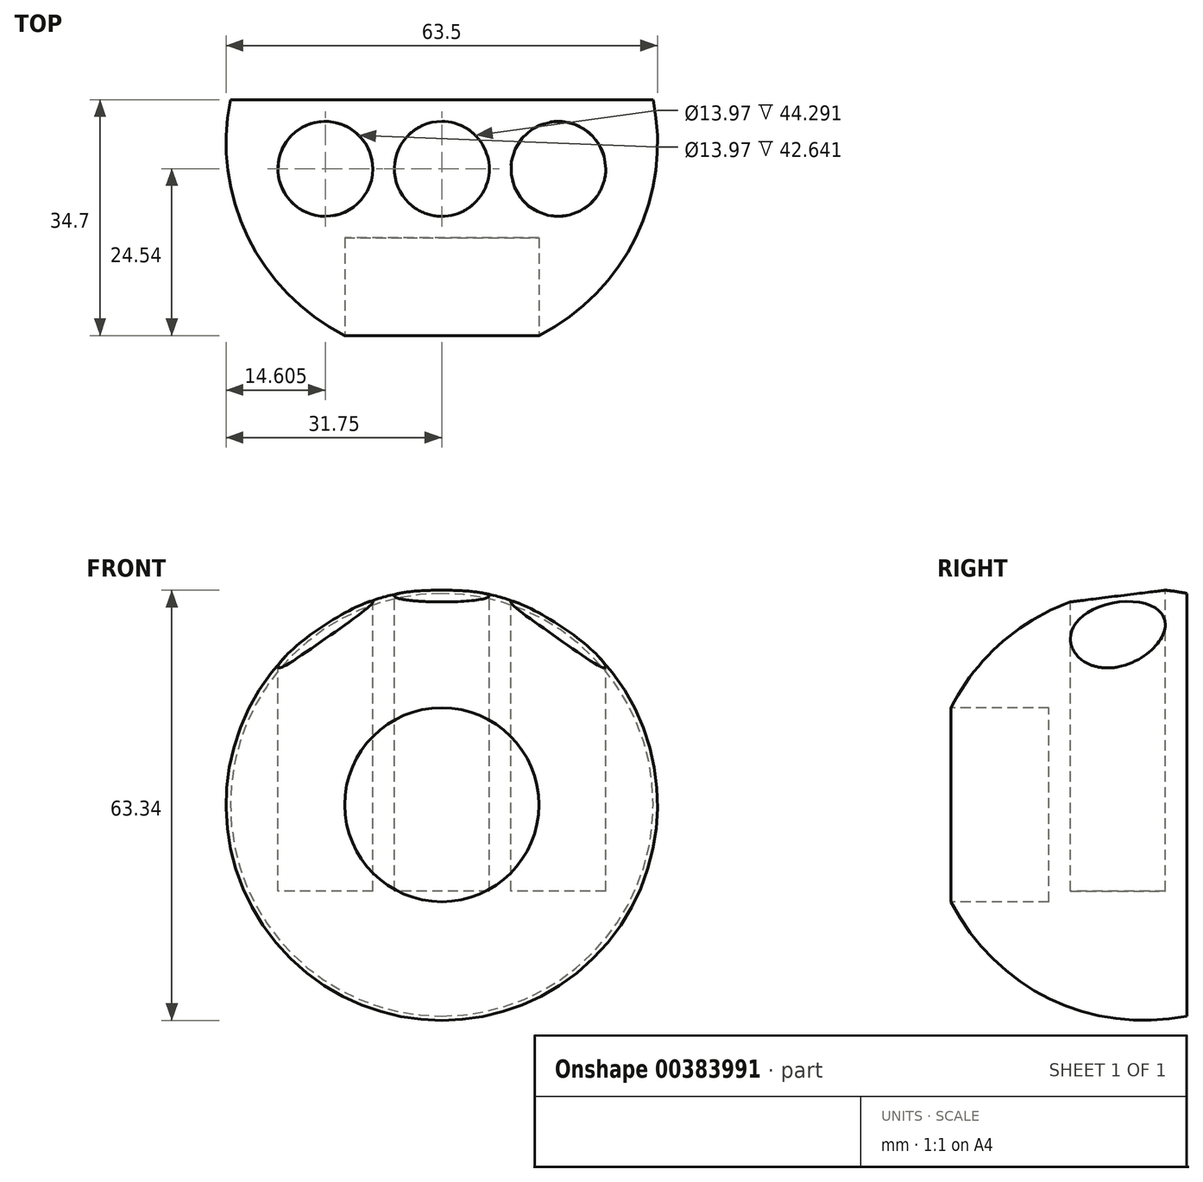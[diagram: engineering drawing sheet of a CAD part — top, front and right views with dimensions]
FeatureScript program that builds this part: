
annotation { "Feature Type Name" : "Feature", "Feature Type Description" : "" }
export const myFeature = defineFeature(function(context is Context, id is Id, definition is map)
    precondition{}
    {
        {
            var Q0;
            Q0=qCreatedBy(makeId("Top.planeOp"),FACE);
            var sketch = newSketch(context, id + "F0", { "sketchPlane" : qUnion([Q0])});
            skCircle(sketch, "E0", {"center": v(0, 0) * mm, "radius": 31.75 * mm});
            skLineSegment(sketch, "E1", {"start": v(0, 31.75) * mm, "end": v(0, -31.75) * mm});
            skSolve(sketch);
        }
        {
            var Q0;
            {var subQ0=sQuery(id+"F0.wireOp",EDGE,"E1");Q0=makeQuery(id+"F0.imprint","IMPRINT",FACE,{"disambiguationData":[TD([[makeQuery(id+"F0.imprint","IMPRINT",EDGE,{"derivedFrom":subQ0}),1.0]])]});}
            var Q1;
            Q1=sQuery(id+"F0.wireOp",EDGE,"E1");
            revolve(context, id + "F1", {"entities" : qUnion([Q0]), "axis" : qUnion([Q1]), "revolveType" : RevolveType.FULL});
        }
        {
            var Q0;
            Q0=qCreatedBy(makeId("Front.planeOp"),FACE);
            cPlane(context, id + "F2", {"entities" : qUnion([Q0]), "cplaneType" : CPlaneType.OFFSET, "offset" : 6.35 * mm, "oppositeDirection" : true, "width" : 152.4 * mm, "height" : 152.4 * mm});
        }
        {
            var Q0;
            Q0=qCreatedBy(id+"F2.planeOp",FACE);
            var sketch = newSketch(context, id + "F3", { "sketchPlane" : qUnion([Q0])});
            skLineSegment(sketch, "E2.bottom", {"start": v(142.6, 118.73) * mm, "end": v(-120.3, 118.73) * mm});
            skLineSegment(sketch, "E2.top", {"start": v(142.6, -87.67) * mm, "end": v(-120.3, -87.67) * mm});
            skLineSegment(sketch, "E2.left", {"start": v(142.6, 118.73) * mm, "end": v(142.6, -87.67) * mm});
            skLineSegment(sketch, "E2.right", {"start": v(-120.3, 118.73) * mm, "end": v(-120.3, -87.67) * mm});
            skSolve(sketch);
        }
        {
            var Q0;
            Q0=makeQuery(id+"F3.imprint","IMPRINT",FACE,{"disambiguationData":[TD([[makeQuery(id+"F3.imprint","IMPRINT",EDGE,{"derivedFrom":sQuery(id+"F3.wireOp",EDGE,"E2.bottom")}),1.0]])]});
            extrude(context, id + "F4", {"entities" : qUnion([Q0]), "operationType" : NewBodyOperationType.REMOVE, "oppositeDirection" : true, "depth" : 25.4 * mm});
        }
        {
            var Q0;
            Q0=qCreatedBy(makeId("Top.planeOp"),FACE);
            cPlane(context, id + "F5", {"entities" : qUnion([Q0]), "cplaneType" : CPlaneType.OFFSET, "offset" : 31.75 * mm, "width" : 152.4 * mm, "height" : 152.4 * mm});
        }
        {
            var Q0;
            Q0=qCreatedBy(id+"F5.planeOp",FACE);
            var sketch = newSketch(context, id + "F6", { "sketchPlane" : qUnion([Q0])});
            skCircle(sketch, "E3", {"center": v(0, -3.81) * mm, "radius": 6.99 * mm});
            skCircle(sketch, "E4", {"center": v(-17.15, -3.81) * mm, "radius": 6.99 * mm});
            skCircle(sketch, "E5", {"center": v(17.15, -3.81) * mm, "radius": 6.99 * mm});
            skSolve(sketch);
        }
        {
            var Q0;
            Q0 = qSketchRegion(id + "F6", true);
            extrude(context, id + "F7", {"entities" : qUnion([Q0]), "operationType" : NewBodyOperationType.REMOVE, "oppositeDirection" : true, "depth" : 44.45 * mm});
        }
        {
            var Q0;
            Q0=qCreatedBy(makeId("Front.planeOp"),FACE);
            cPlane(context, id + "F8", {"entities" : qUnion([Q0]), "cplaneType" : CPlaneType.OFFSET, "offset" : 31.75 * mm, "width" : 152.4 * mm, "height" : 152.4 * mm});
        }
        {
            var Q0;
            Q0=qCreatedBy(id+"F8.planeOp",FACE);
            var sketch = newSketch(context, id + "F9", { "sketchPlane" : qUnion([Q0])});
            skCircle(sketch, "E6", {"center": v(0, 0) * mm, "radius": 14.29 * mm});
            skSolve(sketch);
        }
        {
            var Q0;
            Q0 = qSketchRegion(id + "F9", true);
            extrude(context, id + "F10", {"entities" : qUnion([Q0]), "operationType" : NewBodyOperationType.REMOVE, "oppositeDirection" : true, "depth" : 17.78 * mm});
        }
    });
